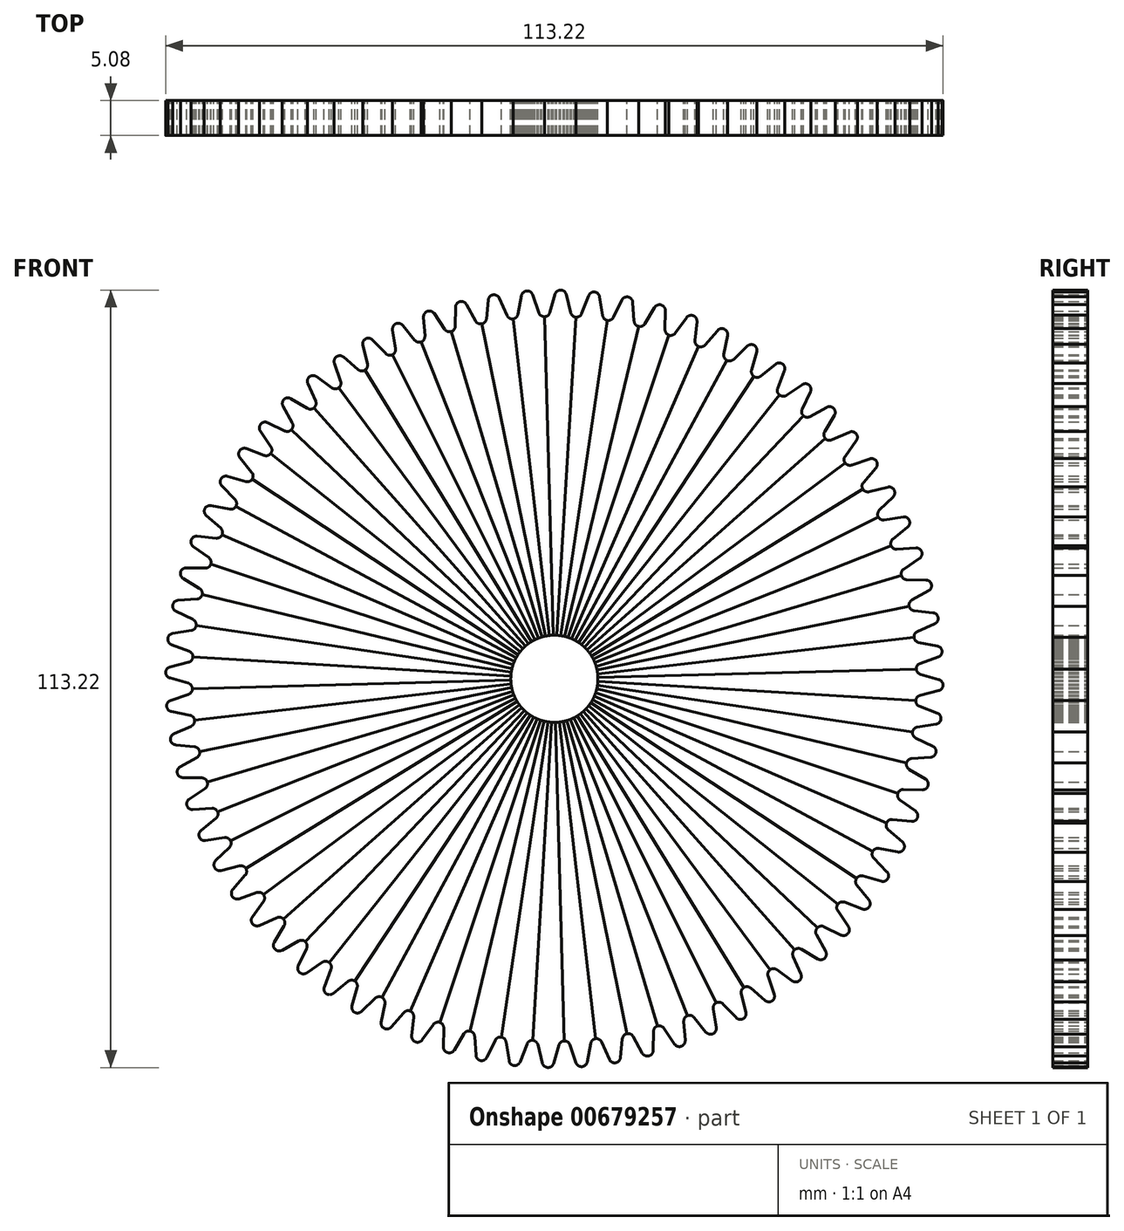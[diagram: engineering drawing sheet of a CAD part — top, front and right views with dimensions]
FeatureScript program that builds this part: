
annotation { "Feature Type Name" : "Feature", "Feature Type Description" : "" }
export const myFeature = defineFeature(function(context is Context, id is Id, definition is map)
    precondition{}
    {
        {
            var Q0;
            Q0=qCreatedBy(makeId("Front.planeOp"),FACE);
            var sketch = newSketch(context, id + "F0", { "sketchPlane" : qUnion([Q0])});
            skLineSegment(sketch, "E0", {"start": v(0, 0) * mm, "end": v(-33.7, 38.01) * mm});
            skLineSegment(sketch, "E1", {"start": v(-34.78, 40.44) * mm, "end": v(-35.92, 42.97) * mm});
            skLineSegment(sketch, "E2", {"start": v(-34.66, 44) * mm, "end": v(-32.41, 42.36) * mm});
            skLineSegment(sketch, "E3", {"start": v(-30.26, 40.8) * mm, "end": v(0, 0) * mm});
            skPoint(sketch, "E4.visualSharp", {"position": v(-37.2, 45.83) * mm});
            skArc(sketch, "E4.filletArc", {"start": v(-34.66, 44) * mm, "mid": v(-35.68, 43.96) * mm, "end": v(-35.92, 42.97) * mm});
            skLineSegment(sketch, "E5", {"start": v(-30.12, 40.61) * mm, "end": v(-31.42, 42.37) * mm});
            skLineSegment(sketch, "E6", {"start": v(-33.7, 38.01) * mm, "end": v(-35.55, 40.1) * mm});
            skPoint(sketch, "E7.visualSharp", {"position": v(-33.7, 38.01) * mm});
            skArc(sketch, "E7.filletArc", {"start": v(-35, 39.47) * mm, "mid": v(-34.73, 39.92) * mm, "end": v(-34.78, 40.44) * mm});
            skPoint(sketch, "E8.visualSharp", {"position": v(-30.26, 40.8) * mm});
            skArc(sketch, "E8.filletArc", {"start": v(-32.41, 42.36) * mm, "mid": v(-31.92, 42.2) * mm, "end": v(-31.42, 42.37) * mm});
            skPoint(sketch, "E9", {"position": v(-35, 39.47) * mm});
            skPoint(sketch, "E10", {"position": v(-31.42, 42.37) * mm});
            skSolve(sketch);
        }
        {
            var Q0;
            Q0=makeQuery(id+"F0.imprint","IMPRINT",FACE,{"disambiguationData":[TD([[makeQuery(id+"F0.imprint","IMPRINT",EDGE,{"derivedFrom":sQuery(id+"F0.wireOp",EDGE,"E0")}),-1.0]])]});
            extrude(context, id + "F1", {"entities" : qUnion([Q0]), "depth" : 5.08 * mm, "offsetDistance" : 25.4 * mm});
        }
        {
            var Q0;
            Q0=makeQuery(id+"F1.opExtrude","SWEPT_BODY",BODY,{"disambiguationData":[OSD([sQuery(id+"F0.wireOp",EDGE,"E0"),sQuery(id+"F0.wireOp",EDGE,"E1"),sQuery(id+"F0.wireOp",EDGE,"E2"),sQuery(id+"F0.wireOp",EDGE,"E3"),sQuery(id+"F0.wireOp",EDGE,"E4.filletArc"),sQuery(id+"F0.wireOp",EDGE,"E5"),sQuery(id+"F0.wireOp",EDGE,"E6"),sQuery(id+"F0.wireOp",EDGE,"E7.filletArc"),sQuery(id+"F0.wireOp",EDGE,"E8.filletArc")])]});
            var Q1;
            Q1=makeQuery(id+"F1.opExtrude","SWEPT_EDGE",EDGE,{"disambiguationData":[OSD([sQuery(id+"F0.wireOp",EDGE,"E0"),sQuery(id+"F0.wireOp",EDGE,"E3")])]});
            circularPattern(context, id + "F2", {"entities" : qUnion([Q0]), "axis" : qUnion([Q1]), "angle" : 360 * degree, "instanceCount" : 72, "equalSpace" : true});
        }
        {
            var Q0;
            Q0=sQuery(id+"F0.wireOp",VERTEX,"E3.end");
            var Q1;
            Q1=makeQuery(id+"F1.opExtrude","SWEPT_BODY",BODY,{"disambiguationData":[OSD([sQuery(id+"F0.wireOp",EDGE,"E0"),sQuery(id+"F0.wireOp",EDGE,"E1"),sQuery(id+"F0.wireOp",EDGE,"E2"),sQuery(id+"F0.wireOp",EDGE,"E3"),sQuery(id+"F0.wireOp",EDGE,"E4.filletArc"),sQuery(id+"F0.wireOp",EDGE,"E5"),sQuery(id+"F0.wireOp",EDGE,"E6"),sQuery(id+"F0.wireOp",EDGE,"E7.filletArc"),sQuery(id+"F0.wireOp",EDGE,"E8.filletArc")])]});
            var Q2;
            Q2=makeQuery(id+"F2.opPattern","COPY",BODY,{"derivedFrom":makeQuery(id+"F1.opExtrude","SWEPT_BODY",BODY,{"disambiguationData":[OSD([sQuery(id+"F0.wireOp",EDGE,"E0"),sQuery(id+"F0.wireOp",EDGE,"E1"),sQuery(id+"F0.wireOp",EDGE,"E2"),sQuery(id+"F0.wireOp",EDGE,"E3"),sQuery(id+"F0.wireOp",EDGE,"E4.filletArc"),sQuery(id+"F0.wireOp",EDGE,"E5"),sQuery(id+"F0.wireOp",EDGE,"E6"),sQuery(id+"F0.wireOp",EDGE,"E7.filletArc"),sQuery(id+"F0.wireOp",EDGE,"E8.filletArc")])]}),"instanceName":"1"});
            var Q3;
            Q3=makeQuery(id+"F2.opPattern","COPY",BODY,{"derivedFrom":makeQuery(id+"F1.opExtrude","SWEPT_BODY",BODY,{"disambiguationData":[OSD([sQuery(id+"F0.wireOp",EDGE,"E0"),sQuery(id+"F0.wireOp",EDGE,"E1"),sQuery(id+"F0.wireOp",EDGE,"E2"),sQuery(id+"F0.wireOp",EDGE,"E3"),sQuery(id+"F0.wireOp",EDGE,"E4.filletArc"),sQuery(id+"F0.wireOp",EDGE,"E5"),sQuery(id+"F0.wireOp",EDGE,"E6"),sQuery(id+"F0.wireOp",EDGE,"E7.filletArc"),sQuery(id+"F0.wireOp",EDGE,"E8.filletArc")])]}),"instanceName":"2"});
            var Q4;
            Q4=makeQuery(id+"F2.opPattern","COPY",BODY,{"derivedFrom":makeQuery(id+"F1.opExtrude","SWEPT_BODY",BODY,{"disambiguationData":[OSD([sQuery(id+"F0.wireOp",EDGE,"E0"),sQuery(id+"F0.wireOp",EDGE,"E1"),sQuery(id+"F0.wireOp",EDGE,"E2"),sQuery(id+"F0.wireOp",EDGE,"E3"),sQuery(id+"F0.wireOp",EDGE,"E4.filletArc"),sQuery(id+"F0.wireOp",EDGE,"E5"),sQuery(id+"F0.wireOp",EDGE,"E6"),sQuery(id+"F0.wireOp",EDGE,"E7.filletArc"),sQuery(id+"F0.wireOp",EDGE,"E8.filletArc")])]}),"instanceName":"3"});
            var Q5;
            Q5=makeQuery(id+"F2.opPattern","COPY",BODY,{"derivedFrom":makeQuery(id+"F1.opExtrude","SWEPT_BODY",BODY,{"disambiguationData":[OSD([sQuery(id+"F0.wireOp",EDGE,"E0"),sQuery(id+"F0.wireOp",EDGE,"E1"),sQuery(id+"F0.wireOp",EDGE,"E2"),sQuery(id+"F0.wireOp",EDGE,"E3"),sQuery(id+"F0.wireOp",EDGE,"E4.filletArc"),sQuery(id+"F0.wireOp",EDGE,"E5"),sQuery(id+"F0.wireOp",EDGE,"E6"),sQuery(id+"F0.wireOp",EDGE,"E7.filletArc"),sQuery(id+"F0.wireOp",EDGE,"E8.filletArc")])]}),"instanceName":"4"});
            var Q6;
            Q6=makeQuery(id+"F2.opPattern","COPY",BODY,{"derivedFrom":makeQuery(id+"F1.opExtrude","SWEPT_BODY",BODY,{"disambiguationData":[OSD([sQuery(id+"F0.wireOp",EDGE,"E0"),sQuery(id+"F0.wireOp",EDGE,"E1"),sQuery(id+"F0.wireOp",EDGE,"E2"),sQuery(id+"F0.wireOp",EDGE,"E3"),sQuery(id+"F0.wireOp",EDGE,"E4.filletArc"),sQuery(id+"F0.wireOp",EDGE,"E5"),sQuery(id+"F0.wireOp",EDGE,"E6"),sQuery(id+"F0.wireOp",EDGE,"E7.filletArc"),sQuery(id+"F0.wireOp",EDGE,"E8.filletArc")])]}),"instanceName":"5"});
            var Q7;
            Q7=makeQuery(id+"F2.opPattern","COPY",BODY,{"derivedFrom":makeQuery(id+"F1.opExtrude","SWEPT_BODY",BODY,{"disambiguationData":[OSD([sQuery(id+"F0.wireOp",EDGE,"E0"),sQuery(id+"F0.wireOp",EDGE,"E1"),sQuery(id+"F0.wireOp",EDGE,"E2"),sQuery(id+"F0.wireOp",EDGE,"E3"),sQuery(id+"F0.wireOp",EDGE,"E4.filletArc"),sQuery(id+"F0.wireOp",EDGE,"E5"),sQuery(id+"F0.wireOp",EDGE,"E6"),sQuery(id+"F0.wireOp",EDGE,"E7.filletArc"),sQuery(id+"F0.wireOp",EDGE,"E8.filletArc")])]}),"instanceName":"6"});
            var Q8;
            Q8=makeQuery(id+"F2.opPattern","COPY",BODY,{"derivedFrom":makeQuery(id+"F1.opExtrude","SWEPT_BODY",BODY,{"disambiguationData":[OSD([sQuery(id+"F0.wireOp",EDGE,"E0"),sQuery(id+"F0.wireOp",EDGE,"E1"),sQuery(id+"F0.wireOp",EDGE,"E2"),sQuery(id+"F0.wireOp",EDGE,"E3"),sQuery(id+"F0.wireOp",EDGE,"E4.filletArc"),sQuery(id+"F0.wireOp",EDGE,"E5"),sQuery(id+"F0.wireOp",EDGE,"E6"),sQuery(id+"F0.wireOp",EDGE,"E7.filletArc"),sQuery(id+"F0.wireOp",EDGE,"E8.filletArc")])]}),"instanceName":"7"});
            var Q9;
            Q9=makeQuery(id+"F2.opPattern","COPY",BODY,{"derivedFrom":makeQuery(id+"F1.opExtrude","SWEPT_BODY",BODY,{"disambiguationData":[OSD([sQuery(id+"F0.wireOp",EDGE,"E0"),sQuery(id+"F0.wireOp",EDGE,"E1"),sQuery(id+"F0.wireOp",EDGE,"E2"),sQuery(id+"F0.wireOp",EDGE,"E3"),sQuery(id+"F0.wireOp",EDGE,"E4.filletArc"),sQuery(id+"F0.wireOp",EDGE,"E5"),sQuery(id+"F0.wireOp",EDGE,"E6"),sQuery(id+"F0.wireOp",EDGE,"E7.filletArc"),sQuery(id+"F0.wireOp",EDGE,"E8.filletArc")])]}),"instanceName":"8"});
            var Q10;
            Q10=makeQuery(id+"F2.opPattern","COPY",BODY,{"derivedFrom":makeQuery(id+"F1.opExtrude","SWEPT_BODY",BODY,{"disambiguationData":[OSD([sQuery(id+"F0.wireOp",EDGE,"E0"),sQuery(id+"F0.wireOp",EDGE,"E1"),sQuery(id+"F0.wireOp",EDGE,"E2"),sQuery(id+"F0.wireOp",EDGE,"E3"),sQuery(id+"F0.wireOp",EDGE,"E4.filletArc"),sQuery(id+"F0.wireOp",EDGE,"E5"),sQuery(id+"F0.wireOp",EDGE,"E6"),sQuery(id+"F0.wireOp",EDGE,"E7.filletArc"),sQuery(id+"F0.wireOp",EDGE,"E8.filletArc")])]}),"instanceName":"9"});
            var Q11;
            Q11=makeQuery(id+"F2.opPattern","COPY",BODY,{"derivedFrom":makeQuery(id+"F1.opExtrude","SWEPT_BODY",BODY,{"disambiguationData":[OSD([sQuery(id+"F0.wireOp",EDGE,"E0"),sQuery(id+"F0.wireOp",EDGE,"E1"),sQuery(id+"F0.wireOp",EDGE,"E2"),sQuery(id+"F0.wireOp",EDGE,"E3"),sQuery(id+"F0.wireOp",EDGE,"E4.filletArc"),sQuery(id+"F0.wireOp",EDGE,"E5"),sQuery(id+"F0.wireOp",EDGE,"E6"),sQuery(id+"F0.wireOp",EDGE,"E7.filletArc"),sQuery(id+"F0.wireOp",EDGE,"E8.filletArc")])]}),"instanceName":"10"});
            var Q12;
            Q12=makeQuery(id+"F2.opPattern","COPY",BODY,{"derivedFrom":makeQuery(id+"F1.opExtrude","SWEPT_BODY",BODY,{"disambiguationData":[OSD([sQuery(id+"F0.wireOp",EDGE,"E0"),sQuery(id+"F0.wireOp",EDGE,"E1"),sQuery(id+"F0.wireOp",EDGE,"E2"),sQuery(id+"F0.wireOp",EDGE,"E3"),sQuery(id+"F0.wireOp",EDGE,"E4.filletArc"),sQuery(id+"F0.wireOp",EDGE,"E5"),sQuery(id+"F0.wireOp",EDGE,"E6"),sQuery(id+"F0.wireOp",EDGE,"E7.filletArc"),sQuery(id+"F0.wireOp",EDGE,"E8.filletArc")])]}),"instanceName":"11"});
            var Q13;
            Q13=makeQuery(id+"F2.opPattern","COPY",BODY,{"derivedFrom":makeQuery(id+"F1.opExtrude","SWEPT_BODY",BODY,{"disambiguationData":[OSD([sQuery(id+"F0.wireOp",EDGE,"E0"),sQuery(id+"F0.wireOp",EDGE,"E1"),sQuery(id+"F0.wireOp",EDGE,"E2"),sQuery(id+"F0.wireOp",EDGE,"E3"),sQuery(id+"F0.wireOp",EDGE,"E4.filletArc"),sQuery(id+"F0.wireOp",EDGE,"E5"),sQuery(id+"F0.wireOp",EDGE,"E6"),sQuery(id+"F0.wireOp",EDGE,"E7.filletArc"),sQuery(id+"F0.wireOp",EDGE,"E8.filletArc")])]}),"instanceName":"12"});
            var Q14;
            Q14=makeQuery(id+"F2.opPattern","COPY",BODY,{"derivedFrom":makeQuery(id+"F1.opExtrude","SWEPT_BODY",BODY,{"disambiguationData":[OSD([sQuery(id+"F0.wireOp",EDGE,"E0"),sQuery(id+"F0.wireOp",EDGE,"E1"),sQuery(id+"F0.wireOp",EDGE,"E2"),sQuery(id+"F0.wireOp",EDGE,"E3"),sQuery(id+"F0.wireOp",EDGE,"E4.filletArc"),sQuery(id+"F0.wireOp",EDGE,"E5"),sQuery(id+"F0.wireOp",EDGE,"E6"),sQuery(id+"F0.wireOp",EDGE,"E7.filletArc"),sQuery(id+"F0.wireOp",EDGE,"E8.filletArc")])]}),"instanceName":"13"});
            var Q15;
            Q15=makeQuery(id+"F2.opPattern","COPY",BODY,{"derivedFrom":makeQuery(id+"F1.opExtrude","SWEPT_BODY",BODY,{"disambiguationData":[OSD([sQuery(id+"F0.wireOp",EDGE,"E0"),sQuery(id+"F0.wireOp",EDGE,"E1"),sQuery(id+"F0.wireOp",EDGE,"E2"),sQuery(id+"F0.wireOp",EDGE,"E3"),sQuery(id+"F0.wireOp",EDGE,"E4.filletArc"),sQuery(id+"F0.wireOp",EDGE,"E5"),sQuery(id+"F0.wireOp",EDGE,"E6"),sQuery(id+"F0.wireOp",EDGE,"E7.filletArc"),sQuery(id+"F0.wireOp",EDGE,"E8.filletArc")])]}),"instanceName":"14"});
            var Q16;
            Q16=makeQuery(id+"F2.opPattern","COPY",BODY,{"derivedFrom":makeQuery(id+"F1.opExtrude","SWEPT_BODY",BODY,{"disambiguationData":[OSD([sQuery(id+"F0.wireOp",EDGE,"E0"),sQuery(id+"F0.wireOp",EDGE,"E1"),sQuery(id+"F0.wireOp",EDGE,"E2"),sQuery(id+"F0.wireOp",EDGE,"E3"),sQuery(id+"F0.wireOp",EDGE,"E4.filletArc"),sQuery(id+"F0.wireOp",EDGE,"E5"),sQuery(id+"F0.wireOp",EDGE,"E6"),sQuery(id+"F0.wireOp",EDGE,"E7.filletArc"),sQuery(id+"F0.wireOp",EDGE,"E8.filletArc")])]}),"instanceName":"15"});
            var Q17;
            Q17=makeQuery(id+"F2.opPattern","COPY",BODY,{"derivedFrom":makeQuery(id+"F1.opExtrude","SWEPT_BODY",BODY,{"disambiguationData":[OSD([sQuery(id+"F0.wireOp",EDGE,"E0"),sQuery(id+"F0.wireOp",EDGE,"E1"),sQuery(id+"F0.wireOp",EDGE,"E2"),sQuery(id+"F0.wireOp",EDGE,"E3"),sQuery(id+"F0.wireOp",EDGE,"E4.filletArc"),sQuery(id+"F0.wireOp",EDGE,"E5"),sQuery(id+"F0.wireOp",EDGE,"E6"),sQuery(id+"F0.wireOp",EDGE,"E7.filletArc"),sQuery(id+"F0.wireOp",EDGE,"E8.filletArc")])]}),"instanceName":"16"});
            var Q18;
            Q18=makeQuery(id+"F2.opPattern","COPY",BODY,{"derivedFrom":makeQuery(id+"F1.opExtrude","SWEPT_BODY",BODY,{"disambiguationData":[OSD([sQuery(id+"F0.wireOp",EDGE,"E0"),sQuery(id+"F0.wireOp",EDGE,"E1"),sQuery(id+"F0.wireOp",EDGE,"E2"),sQuery(id+"F0.wireOp",EDGE,"E3"),sQuery(id+"F0.wireOp",EDGE,"E4.filletArc"),sQuery(id+"F0.wireOp",EDGE,"E5"),sQuery(id+"F0.wireOp",EDGE,"E6"),sQuery(id+"F0.wireOp",EDGE,"E7.filletArc"),sQuery(id+"F0.wireOp",EDGE,"E8.filletArc")])]}),"instanceName":"17"});
            var Q19;
            Q19=makeQuery(id+"F2.opPattern","COPY",BODY,{"derivedFrom":makeQuery(id+"F1.opExtrude","SWEPT_BODY",BODY,{"disambiguationData":[OSD([sQuery(id+"F0.wireOp",EDGE,"E0"),sQuery(id+"F0.wireOp",EDGE,"E1"),sQuery(id+"F0.wireOp",EDGE,"E2"),sQuery(id+"F0.wireOp",EDGE,"E3"),sQuery(id+"F0.wireOp",EDGE,"E4.filletArc"),sQuery(id+"F0.wireOp",EDGE,"E5"),sQuery(id+"F0.wireOp",EDGE,"E6"),sQuery(id+"F0.wireOp",EDGE,"E7.filletArc"),sQuery(id+"F0.wireOp",EDGE,"E8.filletArc")])]}),"instanceName":"18"});
            var Q20;
            Q20=makeQuery(id+"F2.opPattern","COPY",BODY,{"derivedFrom":makeQuery(id+"F1.opExtrude","SWEPT_BODY",BODY,{"disambiguationData":[OSD([sQuery(id+"F0.wireOp",EDGE,"E0"),sQuery(id+"F0.wireOp",EDGE,"E1"),sQuery(id+"F0.wireOp",EDGE,"E2"),sQuery(id+"F0.wireOp",EDGE,"E3"),sQuery(id+"F0.wireOp",EDGE,"E4.filletArc"),sQuery(id+"F0.wireOp",EDGE,"E5"),sQuery(id+"F0.wireOp",EDGE,"E6"),sQuery(id+"F0.wireOp",EDGE,"E7.filletArc"),sQuery(id+"F0.wireOp",EDGE,"E8.filletArc")])]}),"instanceName":"19"});
            var Q21;
            Q21=makeQuery(id+"F2.opPattern","COPY",BODY,{"derivedFrom":makeQuery(id+"F1.opExtrude","SWEPT_BODY",BODY,{"disambiguationData":[OSD([sQuery(id+"F0.wireOp",EDGE,"E0"),sQuery(id+"F0.wireOp",EDGE,"E1"),sQuery(id+"F0.wireOp",EDGE,"E2"),sQuery(id+"F0.wireOp",EDGE,"E3"),sQuery(id+"F0.wireOp",EDGE,"E4.filletArc"),sQuery(id+"F0.wireOp",EDGE,"E5"),sQuery(id+"F0.wireOp",EDGE,"E6"),sQuery(id+"F0.wireOp",EDGE,"E7.filletArc"),sQuery(id+"F0.wireOp",EDGE,"E8.filletArc")])]}),"instanceName":"20"});
            var Q22;
            Q22=makeQuery(id+"F2.opPattern","COPY",BODY,{"derivedFrom":makeQuery(id+"F1.opExtrude","SWEPT_BODY",BODY,{"disambiguationData":[OSD([sQuery(id+"F0.wireOp",EDGE,"E0"),sQuery(id+"F0.wireOp",EDGE,"E1"),sQuery(id+"F0.wireOp",EDGE,"E2"),sQuery(id+"F0.wireOp",EDGE,"E3"),sQuery(id+"F0.wireOp",EDGE,"E4.filletArc"),sQuery(id+"F0.wireOp",EDGE,"E5"),sQuery(id+"F0.wireOp",EDGE,"E6"),sQuery(id+"F0.wireOp",EDGE,"E7.filletArc"),sQuery(id+"F0.wireOp",EDGE,"E8.filletArc")])]}),"instanceName":"21"});
            var Q23;
            Q23=makeQuery(id+"F2.opPattern","COPY",BODY,{"derivedFrom":makeQuery(id+"F1.opExtrude","SWEPT_BODY",BODY,{"disambiguationData":[OSD([sQuery(id+"F0.wireOp",EDGE,"E0"),sQuery(id+"F0.wireOp",EDGE,"E1"),sQuery(id+"F0.wireOp",EDGE,"E2"),sQuery(id+"F0.wireOp",EDGE,"E3"),sQuery(id+"F0.wireOp",EDGE,"E4.filletArc"),sQuery(id+"F0.wireOp",EDGE,"E5"),sQuery(id+"F0.wireOp",EDGE,"E6"),sQuery(id+"F0.wireOp",EDGE,"E7.filletArc"),sQuery(id+"F0.wireOp",EDGE,"E8.filletArc")])]}),"instanceName":"22"});
            var Q24;
            Q24=makeQuery(id+"F2.opPattern","COPY",BODY,{"derivedFrom":makeQuery(id+"F1.opExtrude","SWEPT_BODY",BODY,{"disambiguationData":[OSD([sQuery(id+"F0.wireOp",EDGE,"E0"),sQuery(id+"F0.wireOp",EDGE,"E1"),sQuery(id+"F0.wireOp",EDGE,"E2"),sQuery(id+"F0.wireOp",EDGE,"E3"),sQuery(id+"F0.wireOp",EDGE,"E4.filletArc"),sQuery(id+"F0.wireOp",EDGE,"E5"),sQuery(id+"F0.wireOp",EDGE,"E6"),sQuery(id+"F0.wireOp",EDGE,"E7.filletArc"),sQuery(id+"F0.wireOp",EDGE,"E8.filletArc")])]}),"instanceName":"23"});
            var Q25;
            Q25=makeQuery(id+"F2.opPattern","COPY",BODY,{"derivedFrom":makeQuery(id+"F1.opExtrude","SWEPT_BODY",BODY,{"disambiguationData":[OSD([sQuery(id+"F0.wireOp",EDGE,"E0"),sQuery(id+"F0.wireOp",EDGE,"E1"),sQuery(id+"F0.wireOp",EDGE,"E2"),sQuery(id+"F0.wireOp",EDGE,"E3"),sQuery(id+"F0.wireOp",EDGE,"E4.filletArc"),sQuery(id+"F0.wireOp",EDGE,"E5"),sQuery(id+"F0.wireOp",EDGE,"E6"),sQuery(id+"F0.wireOp",EDGE,"E7.filletArc"),sQuery(id+"F0.wireOp",EDGE,"E8.filletArc")])]}),"instanceName":"24"});
            var Q26;
            Q26=makeQuery(id+"F2.opPattern","COPY",BODY,{"derivedFrom":makeQuery(id+"F1.opExtrude","SWEPT_BODY",BODY,{"disambiguationData":[OSD([sQuery(id+"F0.wireOp",EDGE,"E0"),sQuery(id+"F0.wireOp",EDGE,"E1"),sQuery(id+"F0.wireOp",EDGE,"E2"),sQuery(id+"F0.wireOp",EDGE,"E3"),sQuery(id+"F0.wireOp",EDGE,"E4.filletArc"),sQuery(id+"F0.wireOp",EDGE,"E5"),sQuery(id+"F0.wireOp",EDGE,"E6"),sQuery(id+"F0.wireOp",EDGE,"E7.filletArc"),sQuery(id+"F0.wireOp",EDGE,"E8.filletArc")])]}),"instanceName":"25"});
            var Q27;
            Q27=makeQuery(id+"F2.opPattern","COPY",BODY,{"derivedFrom":makeQuery(id+"F1.opExtrude","SWEPT_BODY",BODY,{"disambiguationData":[OSD([sQuery(id+"F0.wireOp",EDGE,"E0"),sQuery(id+"F0.wireOp",EDGE,"E1"),sQuery(id+"F0.wireOp",EDGE,"E2"),sQuery(id+"F0.wireOp",EDGE,"E3"),sQuery(id+"F0.wireOp",EDGE,"E4.filletArc"),sQuery(id+"F0.wireOp",EDGE,"E5"),sQuery(id+"F0.wireOp",EDGE,"E6"),sQuery(id+"F0.wireOp",EDGE,"E7.filletArc"),sQuery(id+"F0.wireOp",EDGE,"E8.filletArc")])]}),"instanceName":"26"});
            var Q28;
            Q28=makeQuery(id+"F2.opPattern","COPY",BODY,{"derivedFrom":makeQuery(id+"F1.opExtrude","SWEPT_BODY",BODY,{"disambiguationData":[OSD([sQuery(id+"F0.wireOp",EDGE,"E0"),sQuery(id+"F0.wireOp",EDGE,"E1"),sQuery(id+"F0.wireOp",EDGE,"E2"),sQuery(id+"F0.wireOp",EDGE,"E3"),sQuery(id+"F0.wireOp",EDGE,"E4.filletArc"),sQuery(id+"F0.wireOp",EDGE,"E5"),sQuery(id+"F0.wireOp",EDGE,"E6"),sQuery(id+"F0.wireOp",EDGE,"E7.filletArc"),sQuery(id+"F0.wireOp",EDGE,"E8.filletArc")])]}),"instanceName":"27"});
            var Q29;
            Q29=makeQuery(id+"F2.opPattern","COPY",BODY,{"derivedFrom":makeQuery(id+"F1.opExtrude","SWEPT_BODY",BODY,{"disambiguationData":[OSD([sQuery(id+"F0.wireOp",EDGE,"E0"),sQuery(id+"F0.wireOp",EDGE,"E1"),sQuery(id+"F0.wireOp",EDGE,"E2"),sQuery(id+"F0.wireOp",EDGE,"E3"),sQuery(id+"F0.wireOp",EDGE,"E4.filletArc"),sQuery(id+"F0.wireOp",EDGE,"E5"),sQuery(id+"F0.wireOp",EDGE,"E6"),sQuery(id+"F0.wireOp",EDGE,"E7.filletArc"),sQuery(id+"F0.wireOp",EDGE,"E8.filletArc")])]}),"instanceName":"28"});
            var Q30;
            Q30=makeQuery(id+"F2.opPattern","COPY",BODY,{"derivedFrom":makeQuery(id+"F1.opExtrude","SWEPT_BODY",BODY,{"disambiguationData":[OSD([sQuery(id+"F0.wireOp",EDGE,"E0"),sQuery(id+"F0.wireOp",EDGE,"E1"),sQuery(id+"F0.wireOp",EDGE,"E2"),sQuery(id+"F0.wireOp",EDGE,"E3"),sQuery(id+"F0.wireOp",EDGE,"E4.filletArc"),sQuery(id+"F0.wireOp",EDGE,"E5"),sQuery(id+"F0.wireOp",EDGE,"E6"),sQuery(id+"F0.wireOp",EDGE,"E7.filletArc"),sQuery(id+"F0.wireOp",EDGE,"E8.filletArc")])]}),"instanceName":"29"});
            var Q31;
            Q31=makeQuery(id+"F2.opPattern","COPY",BODY,{"derivedFrom":makeQuery(id+"F1.opExtrude","SWEPT_BODY",BODY,{"disambiguationData":[OSD([sQuery(id+"F0.wireOp",EDGE,"E0"),sQuery(id+"F0.wireOp",EDGE,"E1"),sQuery(id+"F0.wireOp",EDGE,"E2"),sQuery(id+"F0.wireOp",EDGE,"E3"),sQuery(id+"F0.wireOp",EDGE,"E4.filletArc"),sQuery(id+"F0.wireOp",EDGE,"E5"),sQuery(id+"F0.wireOp",EDGE,"E6"),sQuery(id+"F0.wireOp",EDGE,"E7.filletArc"),sQuery(id+"F0.wireOp",EDGE,"E8.filletArc")])]}),"instanceName":"30"});
            var Q32;
            Q32=makeQuery(id+"F2.opPattern","COPY",BODY,{"derivedFrom":makeQuery(id+"F1.opExtrude","SWEPT_BODY",BODY,{"disambiguationData":[OSD([sQuery(id+"F0.wireOp",EDGE,"E0"),sQuery(id+"F0.wireOp",EDGE,"E1"),sQuery(id+"F0.wireOp",EDGE,"E2"),sQuery(id+"F0.wireOp",EDGE,"E3"),sQuery(id+"F0.wireOp",EDGE,"E4.filletArc"),sQuery(id+"F0.wireOp",EDGE,"E5"),sQuery(id+"F0.wireOp",EDGE,"E6"),sQuery(id+"F0.wireOp",EDGE,"E7.filletArc"),sQuery(id+"F0.wireOp",EDGE,"E8.filletArc")])]}),"instanceName":"31"});
            var Q33;
            Q33=makeQuery(id+"F2.opPattern","COPY",BODY,{"derivedFrom":makeQuery(id+"F1.opExtrude","SWEPT_BODY",BODY,{"disambiguationData":[OSD([sQuery(id+"F0.wireOp",EDGE,"E0"),sQuery(id+"F0.wireOp",EDGE,"E1"),sQuery(id+"F0.wireOp",EDGE,"E2"),sQuery(id+"F0.wireOp",EDGE,"E3"),sQuery(id+"F0.wireOp",EDGE,"E4.filletArc"),sQuery(id+"F0.wireOp",EDGE,"E5"),sQuery(id+"F0.wireOp",EDGE,"E6"),sQuery(id+"F0.wireOp",EDGE,"E7.filletArc"),sQuery(id+"F0.wireOp",EDGE,"E8.filletArc")])]}),"instanceName":"32"});
            var Q34;
            Q34=makeQuery(id+"F2.opPattern","COPY",BODY,{"derivedFrom":makeQuery(id+"F1.opExtrude","SWEPT_BODY",BODY,{"disambiguationData":[OSD([sQuery(id+"F0.wireOp",EDGE,"E0"),sQuery(id+"F0.wireOp",EDGE,"E1"),sQuery(id+"F0.wireOp",EDGE,"E2"),sQuery(id+"F0.wireOp",EDGE,"E3"),sQuery(id+"F0.wireOp",EDGE,"E4.filletArc"),sQuery(id+"F0.wireOp",EDGE,"E5"),sQuery(id+"F0.wireOp",EDGE,"E6"),sQuery(id+"F0.wireOp",EDGE,"E7.filletArc"),sQuery(id+"F0.wireOp",EDGE,"E8.filletArc")])]}),"instanceName":"33"});
            var Q35;
            Q35=makeQuery(id+"F2.opPattern","COPY",BODY,{"derivedFrom":makeQuery(id+"F1.opExtrude","SWEPT_BODY",BODY,{"disambiguationData":[OSD([sQuery(id+"F0.wireOp",EDGE,"E0"),sQuery(id+"F0.wireOp",EDGE,"E1"),sQuery(id+"F0.wireOp",EDGE,"E2"),sQuery(id+"F0.wireOp",EDGE,"E3"),sQuery(id+"F0.wireOp",EDGE,"E4.filletArc"),sQuery(id+"F0.wireOp",EDGE,"E5"),sQuery(id+"F0.wireOp",EDGE,"E6"),sQuery(id+"F0.wireOp",EDGE,"E7.filletArc"),sQuery(id+"F0.wireOp",EDGE,"E8.filletArc")])]}),"instanceName":"34"});
            var Q36;
            Q36=makeQuery(id+"F2.opPattern","COPY",BODY,{"derivedFrom":makeQuery(id+"F1.opExtrude","SWEPT_BODY",BODY,{"disambiguationData":[OSD([sQuery(id+"F0.wireOp",EDGE,"E0"),sQuery(id+"F0.wireOp",EDGE,"E1"),sQuery(id+"F0.wireOp",EDGE,"E2"),sQuery(id+"F0.wireOp",EDGE,"E3"),sQuery(id+"F0.wireOp",EDGE,"E4.filletArc"),sQuery(id+"F0.wireOp",EDGE,"E5"),sQuery(id+"F0.wireOp",EDGE,"E6"),sQuery(id+"F0.wireOp",EDGE,"E7.filletArc"),sQuery(id+"F0.wireOp",EDGE,"E8.filletArc")])]}),"instanceName":"35"});
            var Q37;
            Q37=makeQuery(id+"F2.opPattern","COPY",BODY,{"derivedFrom":makeQuery(id+"F1.opExtrude","SWEPT_BODY",BODY,{"disambiguationData":[OSD([sQuery(id+"F0.wireOp",EDGE,"E0"),sQuery(id+"F0.wireOp",EDGE,"E1"),sQuery(id+"F0.wireOp",EDGE,"E2"),sQuery(id+"F0.wireOp",EDGE,"E3"),sQuery(id+"F0.wireOp",EDGE,"E4.filletArc"),sQuery(id+"F0.wireOp",EDGE,"E5"),sQuery(id+"F0.wireOp",EDGE,"E6"),sQuery(id+"F0.wireOp",EDGE,"E7.filletArc"),sQuery(id+"F0.wireOp",EDGE,"E8.filletArc")])]}),"instanceName":"36"});
            var Q38;
            Q38=makeQuery(id+"F2.opPattern","COPY",BODY,{"derivedFrom":makeQuery(id+"F1.opExtrude","SWEPT_BODY",BODY,{"disambiguationData":[OSD([sQuery(id+"F0.wireOp",EDGE,"E0"),sQuery(id+"F0.wireOp",EDGE,"E1"),sQuery(id+"F0.wireOp",EDGE,"E2"),sQuery(id+"F0.wireOp",EDGE,"E3"),sQuery(id+"F0.wireOp",EDGE,"E4.filletArc"),sQuery(id+"F0.wireOp",EDGE,"E5"),sQuery(id+"F0.wireOp",EDGE,"E6"),sQuery(id+"F0.wireOp",EDGE,"E7.filletArc"),sQuery(id+"F0.wireOp",EDGE,"E8.filletArc")])]}),"instanceName":"37"});
            var Q39;
            Q39=makeQuery(id+"F2.opPattern","COPY",BODY,{"derivedFrom":makeQuery(id+"F1.opExtrude","SWEPT_BODY",BODY,{"disambiguationData":[OSD([sQuery(id+"F0.wireOp",EDGE,"E0"),sQuery(id+"F0.wireOp",EDGE,"E1"),sQuery(id+"F0.wireOp",EDGE,"E2"),sQuery(id+"F0.wireOp",EDGE,"E3"),sQuery(id+"F0.wireOp",EDGE,"E4.filletArc"),sQuery(id+"F0.wireOp",EDGE,"E5"),sQuery(id+"F0.wireOp",EDGE,"E6"),sQuery(id+"F0.wireOp",EDGE,"E7.filletArc"),sQuery(id+"F0.wireOp",EDGE,"E8.filletArc")])]}),"instanceName":"38"});
            var Q40;
            Q40=makeQuery(id+"F2.opPattern","COPY",BODY,{"derivedFrom":makeQuery(id+"F1.opExtrude","SWEPT_BODY",BODY,{"disambiguationData":[OSD([sQuery(id+"F0.wireOp",EDGE,"E0"),sQuery(id+"F0.wireOp",EDGE,"E1"),sQuery(id+"F0.wireOp",EDGE,"E2"),sQuery(id+"F0.wireOp",EDGE,"E3"),sQuery(id+"F0.wireOp",EDGE,"E4.filletArc"),sQuery(id+"F0.wireOp",EDGE,"E5"),sQuery(id+"F0.wireOp",EDGE,"E6"),sQuery(id+"F0.wireOp",EDGE,"E7.filletArc"),sQuery(id+"F0.wireOp",EDGE,"E8.filletArc")])]}),"instanceName":"39"});
            var Q41;
            Q41=makeQuery(id+"F2.opPattern","COPY",BODY,{"derivedFrom":makeQuery(id+"F1.opExtrude","SWEPT_BODY",BODY,{"disambiguationData":[OSD([sQuery(id+"F0.wireOp",EDGE,"E0"),sQuery(id+"F0.wireOp",EDGE,"E1"),sQuery(id+"F0.wireOp",EDGE,"E2"),sQuery(id+"F0.wireOp",EDGE,"E3"),sQuery(id+"F0.wireOp",EDGE,"E4.filletArc"),sQuery(id+"F0.wireOp",EDGE,"E5"),sQuery(id+"F0.wireOp",EDGE,"E6"),sQuery(id+"F0.wireOp",EDGE,"E7.filletArc"),sQuery(id+"F0.wireOp",EDGE,"E8.filletArc")])]}),"instanceName":"40"});
            var Q42;
            Q42=makeQuery(id+"F2.opPattern","COPY",BODY,{"derivedFrom":makeQuery(id+"F1.opExtrude","SWEPT_BODY",BODY,{"disambiguationData":[OSD([sQuery(id+"F0.wireOp",EDGE,"E0"),sQuery(id+"F0.wireOp",EDGE,"E1"),sQuery(id+"F0.wireOp",EDGE,"E2"),sQuery(id+"F0.wireOp",EDGE,"E3"),sQuery(id+"F0.wireOp",EDGE,"E4.filletArc"),sQuery(id+"F0.wireOp",EDGE,"E5"),sQuery(id+"F0.wireOp",EDGE,"E6"),sQuery(id+"F0.wireOp",EDGE,"E7.filletArc"),sQuery(id+"F0.wireOp",EDGE,"E8.filletArc")])]}),"instanceName":"41"});
            var Q43;
            Q43=makeQuery(id+"F2.opPattern","COPY",BODY,{"derivedFrom":makeQuery(id+"F1.opExtrude","SWEPT_BODY",BODY,{"disambiguationData":[OSD([sQuery(id+"F0.wireOp",EDGE,"E0"),sQuery(id+"F0.wireOp",EDGE,"E1"),sQuery(id+"F0.wireOp",EDGE,"E2"),sQuery(id+"F0.wireOp",EDGE,"E3"),sQuery(id+"F0.wireOp",EDGE,"E4.filletArc"),sQuery(id+"F0.wireOp",EDGE,"E5"),sQuery(id+"F0.wireOp",EDGE,"E6"),sQuery(id+"F0.wireOp",EDGE,"E7.filletArc"),sQuery(id+"F0.wireOp",EDGE,"E8.filletArc")])]}),"instanceName":"42"});
            var Q44;
            Q44=makeQuery(id+"F2.opPattern","COPY",BODY,{"derivedFrom":makeQuery(id+"F1.opExtrude","SWEPT_BODY",BODY,{"disambiguationData":[OSD([sQuery(id+"F0.wireOp",EDGE,"E0"),sQuery(id+"F0.wireOp",EDGE,"E1"),sQuery(id+"F0.wireOp",EDGE,"E2"),sQuery(id+"F0.wireOp",EDGE,"E3"),sQuery(id+"F0.wireOp",EDGE,"E4.filletArc"),sQuery(id+"F0.wireOp",EDGE,"E5"),sQuery(id+"F0.wireOp",EDGE,"E6"),sQuery(id+"F0.wireOp",EDGE,"E7.filletArc"),sQuery(id+"F0.wireOp",EDGE,"E8.filletArc")])]}),"instanceName":"43"});
            var Q45;
            Q45=makeQuery(id+"F2.opPattern","COPY",BODY,{"derivedFrom":makeQuery(id+"F1.opExtrude","SWEPT_BODY",BODY,{"disambiguationData":[OSD([sQuery(id+"F0.wireOp",EDGE,"E0"),sQuery(id+"F0.wireOp",EDGE,"E1"),sQuery(id+"F0.wireOp",EDGE,"E2"),sQuery(id+"F0.wireOp",EDGE,"E3"),sQuery(id+"F0.wireOp",EDGE,"E4.filletArc"),sQuery(id+"F0.wireOp",EDGE,"E5"),sQuery(id+"F0.wireOp",EDGE,"E6"),sQuery(id+"F0.wireOp",EDGE,"E7.filletArc"),sQuery(id+"F0.wireOp",EDGE,"E8.filletArc")])]}),"instanceName":"44"});
            var Q46;
            Q46=makeQuery(id+"F2.opPattern","COPY",BODY,{"derivedFrom":makeQuery(id+"F1.opExtrude","SWEPT_BODY",BODY,{"disambiguationData":[OSD([sQuery(id+"F0.wireOp",EDGE,"E0"),sQuery(id+"F0.wireOp",EDGE,"E1"),sQuery(id+"F0.wireOp",EDGE,"E2"),sQuery(id+"F0.wireOp",EDGE,"E3"),sQuery(id+"F0.wireOp",EDGE,"E4.filletArc"),sQuery(id+"F0.wireOp",EDGE,"E5"),sQuery(id+"F0.wireOp",EDGE,"E6"),sQuery(id+"F0.wireOp",EDGE,"E7.filletArc"),sQuery(id+"F0.wireOp",EDGE,"E8.filletArc")])]}),"instanceName":"45"});
            var Q47;
            Q47=makeQuery(id+"F2.opPattern","COPY",BODY,{"derivedFrom":makeQuery(id+"F1.opExtrude","SWEPT_BODY",BODY,{"disambiguationData":[OSD([sQuery(id+"F0.wireOp",EDGE,"E0"),sQuery(id+"F0.wireOp",EDGE,"E1"),sQuery(id+"F0.wireOp",EDGE,"E2"),sQuery(id+"F0.wireOp",EDGE,"E3"),sQuery(id+"F0.wireOp",EDGE,"E4.filletArc"),sQuery(id+"F0.wireOp",EDGE,"E5"),sQuery(id+"F0.wireOp",EDGE,"E6"),sQuery(id+"F0.wireOp",EDGE,"E7.filletArc"),sQuery(id+"F0.wireOp",EDGE,"E8.filletArc")])]}),"instanceName":"46"});
            var Q48;
            Q48=makeQuery(id+"F2.opPattern","COPY",BODY,{"derivedFrom":makeQuery(id+"F1.opExtrude","SWEPT_BODY",BODY,{"disambiguationData":[OSD([sQuery(id+"F0.wireOp",EDGE,"E0"),sQuery(id+"F0.wireOp",EDGE,"E1"),sQuery(id+"F0.wireOp",EDGE,"E2"),sQuery(id+"F0.wireOp",EDGE,"E3"),sQuery(id+"F0.wireOp",EDGE,"E4.filletArc"),sQuery(id+"F0.wireOp",EDGE,"E5"),sQuery(id+"F0.wireOp",EDGE,"E6"),sQuery(id+"F0.wireOp",EDGE,"E7.filletArc"),sQuery(id+"F0.wireOp",EDGE,"E8.filletArc")])]}),"instanceName":"47"});
            var Q49;
            Q49=makeQuery(id+"F2.opPattern","COPY",BODY,{"derivedFrom":makeQuery(id+"F1.opExtrude","SWEPT_BODY",BODY,{"disambiguationData":[OSD([sQuery(id+"F0.wireOp",EDGE,"E0"),sQuery(id+"F0.wireOp",EDGE,"E1"),sQuery(id+"F0.wireOp",EDGE,"E2"),sQuery(id+"F0.wireOp",EDGE,"E3"),sQuery(id+"F0.wireOp",EDGE,"E4.filletArc"),sQuery(id+"F0.wireOp",EDGE,"E5"),sQuery(id+"F0.wireOp",EDGE,"E6"),sQuery(id+"F0.wireOp",EDGE,"E7.filletArc"),sQuery(id+"F0.wireOp",EDGE,"E8.filletArc")])]}),"instanceName":"48"});
            var Q50;
            Q50=makeQuery(id+"F2.opPattern","COPY",BODY,{"derivedFrom":makeQuery(id+"F1.opExtrude","SWEPT_BODY",BODY,{"disambiguationData":[OSD([sQuery(id+"F0.wireOp",EDGE,"E0"),sQuery(id+"F0.wireOp",EDGE,"E1"),sQuery(id+"F0.wireOp",EDGE,"E2"),sQuery(id+"F0.wireOp",EDGE,"E3"),sQuery(id+"F0.wireOp",EDGE,"E4.filletArc"),sQuery(id+"F0.wireOp",EDGE,"E5"),sQuery(id+"F0.wireOp",EDGE,"E6"),sQuery(id+"F0.wireOp",EDGE,"E7.filletArc"),sQuery(id+"F0.wireOp",EDGE,"E8.filletArc")])]}),"instanceName":"49"});
            var Q51;
            Q51=makeQuery(id+"F2.opPattern","COPY",BODY,{"derivedFrom":makeQuery(id+"F1.opExtrude","SWEPT_BODY",BODY,{"disambiguationData":[OSD([sQuery(id+"F0.wireOp",EDGE,"E0"),sQuery(id+"F0.wireOp",EDGE,"E1"),sQuery(id+"F0.wireOp",EDGE,"E2"),sQuery(id+"F0.wireOp",EDGE,"E3"),sQuery(id+"F0.wireOp",EDGE,"E4.filletArc"),sQuery(id+"F0.wireOp",EDGE,"E5"),sQuery(id+"F0.wireOp",EDGE,"E6"),sQuery(id+"F0.wireOp",EDGE,"E7.filletArc"),sQuery(id+"F0.wireOp",EDGE,"E8.filletArc")])]}),"instanceName":"50"});
            var Q52;
            Q52=makeQuery(id+"F2.opPattern","COPY",BODY,{"derivedFrom":makeQuery(id+"F1.opExtrude","SWEPT_BODY",BODY,{"disambiguationData":[OSD([sQuery(id+"F0.wireOp",EDGE,"E0"),sQuery(id+"F0.wireOp",EDGE,"E1"),sQuery(id+"F0.wireOp",EDGE,"E2"),sQuery(id+"F0.wireOp",EDGE,"E3"),sQuery(id+"F0.wireOp",EDGE,"E4.filletArc"),sQuery(id+"F0.wireOp",EDGE,"E5"),sQuery(id+"F0.wireOp",EDGE,"E6"),sQuery(id+"F0.wireOp",EDGE,"E7.filletArc"),sQuery(id+"F0.wireOp",EDGE,"E8.filletArc")])]}),"instanceName":"51"});
            var Q53;
            Q53=makeQuery(id+"F2.opPattern","COPY",BODY,{"derivedFrom":makeQuery(id+"F1.opExtrude","SWEPT_BODY",BODY,{"disambiguationData":[OSD([sQuery(id+"F0.wireOp",EDGE,"E0"),sQuery(id+"F0.wireOp",EDGE,"E1"),sQuery(id+"F0.wireOp",EDGE,"E2"),sQuery(id+"F0.wireOp",EDGE,"E3"),sQuery(id+"F0.wireOp",EDGE,"E4.filletArc"),sQuery(id+"F0.wireOp",EDGE,"E5"),sQuery(id+"F0.wireOp",EDGE,"E6"),sQuery(id+"F0.wireOp",EDGE,"E7.filletArc"),sQuery(id+"F0.wireOp",EDGE,"E8.filletArc")])]}),"instanceName":"52"});
            var Q54;
            Q54=makeQuery(id+"F2.opPattern","COPY",BODY,{"derivedFrom":makeQuery(id+"F1.opExtrude","SWEPT_BODY",BODY,{"disambiguationData":[OSD([sQuery(id+"F0.wireOp",EDGE,"E0"),sQuery(id+"F0.wireOp",EDGE,"E1"),sQuery(id+"F0.wireOp",EDGE,"E2"),sQuery(id+"F0.wireOp",EDGE,"E3"),sQuery(id+"F0.wireOp",EDGE,"E4.filletArc"),sQuery(id+"F0.wireOp",EDGE,"E5"),sQuery(id+"F0.wireOp",EDGE,"E6"),sQuery(id+"F0.wireOp",EDGE,"E7.filletArc"),sQuery(id+"F0.wireOp",EDGE,"E8.filletArc")])]}),"instanceName":"53"});
            var Q55;
            Q55=makeQuery(id+"F2.opPattern","COPY",BODY,{"derivedFrom":makeQuery(id+"F1.opExtrude","SWEPT_BODY",BODY,{"disambiguationData":[OSD([sQuery(id+"F0.wireOp",EDGE,"E0"),sQuery(id+"F0.wireOp",EDGE,"E1"),sQuery(id+"F0.wireOp",EDGE,"E2"),sQuery(id+"F0.wireOp",EDGE,"E3"),sQuery(id+"F0.wireOp",EDGE,"E4.filletArc"),sQuery(id+"F0.wireOp",EDGE,"E5"),sQuery(id+"F0.wireOp",EDGE,"E6"),sQuery(id+"F0.wireOp",EDGE,"E7.filletArc"),sQuery(id+"F0.wireOp",EDGE,"E8.filletArc")])]}),"instanceName":"54"});
            var Q56;
            Q56=makeQuery(id+"F2.opPattern","COPY",BODY,{"derivedFrom":makeQuery(id+"F1.opExtrude","SWEPT_BODY",BODY,{"disambiguationData":[OSD([sQuery(id+"F0.wireOp",EDGE,"E0"),sQuery(id+"F0.wireOp",EDGE,"E1"),sQuery(id+"F0.wireOp",EDGE,"E2"),sQuery(id+"F0.wireOp",EDGE,"E3"),sQuery(id+"F0.wireOp",EDGE,"E4.filletArc"),sQuery(id+"F0.wireOp",EDGE,"E5"),sQuery(id+"F0.wireOp",EDGE,"E6"),sQuery(id+"F0.wireOp",EDGE,"E7.filletArc"),sQuery(id+"F0.wireOp",EDGE,"E8.filletArc")])]}),"instanceName":"55"});
            var Q57;
            Q57=makeQuery(id+"F2.opPattern","COPY",BODY,{"derivedFrom":makeQuery(id+"F1.opExtrude","SWEPT_BODY",BODY,{"disambiguationData":[OSD([sQuery(id+"F0.wireOp",EDGE,"E0"),sQuery(id+"F0.wireOp",EDGE,"E1"),sQuery(id+"F0.wireOp",EDGE,"E2"),sQuery(id+"F0.wireOp",EDGE,"E3"),sQuery(id+"F0.wireOp",EDGE,"E4.filletArc"),sQuery(id+"F0.wireOp",EDGE,"E5"),sQuery(id+"F0.wireOp",EDGE,"E6"),sQuery(id+"F0.wireOp",EDGE,"E7.filletArc"),sQuery(id+"F0.wireOp",EDGE,"E8.filletArc")])]}),"instanceName":"56"});
            var Q58;
            Q58=makeQuery(id+"F2.opPattern","COPY",BODY,{"derivedFrom":makeQuery(id+"F1.opExtrude","SWEPT_BODY",BODY,{"disambiguationData":[OSD([sQuery(id+"F0.wireOp",EDGE,"E0"),sQuery(id+"F0.wireOp",EDGE,"E1"),sQuery(id+"F0.wireOp",EDGE,"E2"),sQuery(id+"F0.wireOp",EDGE,"E3"),sQuery(id+"F0.wireOp",EDGE,"E4.filletArc"),sQuery(id+"F0.wireOp",EDGE,"E5"),sQuery(id+"F0.wireOp",EDGE,"E6"),sQuery(id+"F0.wireOp",EDGE,"E7.filletArc"),sQuery(id+"F0.wireOp",EDGE,"E8.filletArc")])]}),"instanceName":"57"});
            var Q59;
            Q59=makeQuery(id+"F2.opPattern","COPY",BODY,{"derivedFrom":makeQuery(id+"F1.opExtrude","SWEPT_BODY",BODY,{"disambiguationData":[OSD([sQuery(id+"F0.wireOp",EDGE,"E0"),sQuery(id+"F0.wireOp",EDGE,"E1"),sQuery(id+"F0.wireOp",EDGE,"E2"),sQuery(id+"F0.wireOp",EDGE,"E3"),sQuery(id+"F0.wireOp",EDGE,"E4.filletArc"),sQuery(id+"F0.wireOp",EDGE,"E5"),sQuery(id+"F0.wireOp",EDGE,"E6"),sQuery(id+"F0.wireOp",EDGE,"E7.filletArc"),sQuery(id+"F0.wireOp",EDGE,"E8.filletArc")])]}),"instanceName":"58"});
            var Q60;
            Q60=makeQuery(id+"F2.opPattern","COPY",BODY,{"derivedFrom":makeQuery(id+"F1.opExtrude","SWEPT_BODY",BODY,{"disambiguationData":[OSD([sQuery(id+"F0.wireOp",EDGE,"E0"),sQuery(id+"F0.wireOp",EDGE,"E1"),sQuery(id+"F0.wireOp",EDGE,"E2"),sQuery(id+"F0.wireOp",EDGE,"E3"),sQuery(id+"F0.wireOp",EDGE,"E4.filletArc"),sQuery(id+"F0.wireOp",EDGE,"E5"),sQuery(id+"F0.wireOp",EDGE,"E6"),sQuery(id+"F0.wireOp",EDGE,"E7.filletArc"),sQuery(id+"F0.wireOp",EDGE,"E8.filletArc")])]}),"instanceName":"59"});
            var Q61;
            Q61=makeQuery(id+"F2.opPattern","COPY",BODY,{"derivedFrom":makeQuery(id+"F1.opExtrude","SWEPT_BODY",BODY,{"disambiguationData":[OSD([sQuery(id+"F0.wireOp",EDGE,"E0"),sQuery(id+"F0.wireOp",EDGE,"E1"),sQuery(id+"F0.wireOp",EDGE,"E2"),sQuery(id+"F0.wireOp",EDGE,"E3"),sQuery(id+"F0.wireOp",EDGE,"E4.filletArc"),sQuery(id+"F0.wireOp",EDGE,"E5"),sQuery(id+"F0.wireOp",EDGE,"E6"),sQuery(id+"F0.wireOp",EDGE,"E7.filletArc"),sQuery(id+"F0.wireOp",EDGE,"E8.filletArc")])]}),"instanceName":"60"});
            var Q62;
            Q62=makeQuery(id+"F2.opPattern","COPY",BODY,{"derivedFrom":makeQuery(id+"F1.opExtrude","SWEPT_BODY",BODY,{"disambiguationData":[OSD([sQuery(id+"F0.wireOp",EDGE,"E0"),sQuery(id+"F0.wireOp",EDGE,"E1"),sQuery(id+"F0.wireOp",EDGE,"E2"),sQuery(id+"F0.wireOp",EDGE,"E3"),sQuery(id+"F0.wireOp",EDGE,"E4.filletArc"),sQuery(id+"F0.wireOp",EDGE,"E5"),sQuery(id+"F0.wireOp",EDGE,"E6"),sQuery(id+"F0.wireOp",EDGE,"E7.filletArc"),sQuery(id+"F0.wireOp",EDGE,"E8.filletArc")])]}),"instanceName":"61"});
            var Q63;
            Q63=makeQuery(id+"F2.opPattern","COPY",BODY,{"derivedFrom":makeQuery(id+"F1.opExtrude","SWEPT_BODY",BODY,{"disambiguationData":[OSD([sQuery(id+"F0.wireOp",EDGE,"E0"),sQuery(id+"F0.wireOp",EDGE,"E1"),sQuery(id+"F0.wireOp",EDGE,"E2"),sQuery(id+"F0.wireOp",EDGE,"E3"),sQuery(id+"F0.wireOp",EDGE,"E4.filletArc"),sQuery(id+"F0.wireOp",EDGE,"E5"),sQuery(id+"F0.wireOp",EDGE,"E6"),sQuery(id+"F0.wireOp",EDGE,"E7.filletArc"),sQuery(id+"F0.wireOp",EDGE,"E8.filletArc")])]}),"instanceName":"62"});
            var Q64;
            Q64=makeQuery(id+"F2.opPattern","COPY",BODY,{"derivedFrom":makeQuery(id+"F1.opExtrude","SWEPT_BODY",BODY,{"disambiguationData":[OSD([sQuery(id+"F0.wireOp",EDGE,"E0"),sQuery(id+"F0.wireOp",EDGE,"E1"),sQuery(id+"F0.wireOp",EDGE,"E2"),sQuery(id+"F0.wireOp",EDGE,"E3"),sQuery(id+"F0.wireOp",EDGE,"E4.filletArc"),sQuery(id+"F0.wireOp",EDGE,"E5"),sQuery(id+"F0.wireOp",EDGE,"E6"),sQuery(id+"F0.wireOp",EDGE,"E7.filletArc"),sQuery(id+"F0.wireOp",EDGE,"E8.filletArc")])]}),"instanceName":"63"});
            var Q65;
            Q65=makeQuery(id+"F2.opPattern","COPY",BODY,{"derivedFrom":makeQuery(id+"F1.opExtrude","SWEPT_BODY",BODY,{"disambiguationData":[OSD([sQuery(id+"F0.wireOp",EDGE,"E0"),sQuery(id+"F0.wireOp",EDGE,"E1"),sQuery(id+"F0.wireOp",EDGE,"E2"),sQuery(id+"F0.wireOp",EDGE,"E3"),sQuery(id+"F0.wireOp",EDGE,"E4.filletArc"),sQuery(id+"F0.wireOp",EDGE,"E5"),sQuery(id+"F0.wireOp",EDGE,"E6"),sQuery(id+"F0.wireOp",EDGE,"E7.filletArc"),sQuery(id+"F0.wireOp",EDGE,"E8.filletArc")])]}),"instanceName":"64"});
            var Q66;
            Q66=makeQuery(id+"F2.opPattern","COPY",BODY,{"derivedFrom":makeQuery(id+"F1.opExtrude","SWEPT_BODY",BODY,{"disambiguationData":[OSD([sQuery(id+"F0.wireOp",EDGE,"E0"),sQuery(id+"F0.wireOp",EDGE,"E1"),sQuery(id+"F0.wireOp",EDGE,"E2"),sQuery(id+"F0.wireOp",EDGE,"E3"),sQuery(id+"F0.wireOp",EDGE,"E4.filletArc"),sQuery(id+"F0.wireOp",EDGE,"E5"),sQuery(id+"F0.wireOp",EDGE,"E6"),sQuery(id+"F0.wireOp",EDGE,"E7.filletArc"),sQuery(id+"F0.wireOp",EDGE,"E8.filletArc")])]}),"instanceName":"65"});
            var Q67;
            Q67=makeQuery(id+"F2.opPattern","COPY",BODY,{"derivedFrom":makeQuery(id+"F1.opExtrude","SWEPT_BODY",BODY,{"disambiguationData":[OSD([sQuery(id+"F0.wireOp",EDGE,"E0"),sQuery(id+"F0.wireOp",EDGE,"E1"),sQuery(id+"F0.wireOp",EDGE,"E2"),sQuery(id+"F0.wireOp",EDGE,"E3"),sQuery(id+"F0.wireOp",EDGE,"E4.filletArc"),sQuery(id+"F0.wireOp",EDGE,"E5"),sQuery(id+"F0.wireOp",EDGE,"E6"),sQuery(id+"F0.wireOp",EDGE,"E7.filletArc"),sQuery(id+"F0.wireOp",EDGE,"E8.filletArc")])]}),"instanceName":"66"});
            var Q68;
            Q68=makeQuery(id+"F2.opPattern","COPY",BODY,{"derivedFrom":makeQuery(id+"F1.opExtrude","SWEPT_BODY",BODY,{"disambiguationData":[OSD([sQuery(id+"F0.wireOp",EDGE,"E0"),sQuery(id+"F0.wireOp",EDGE,"E1"),sQuery(id+"F0.wireOp",EDGE,"E2"),sQuery(id+"F0.wireOp",EDGE,"E3"),sQuery(id+"F0.wireOp",EDGE,"E4.filletArc"),sQuery(id+"F0.wireOp",EDGE,"E5"),sQuery(id+"F0.wireOp",EDGE,"E6"),sQuery(id+"F0.wireOp",EDGE,"E7.filletArc"),sQuery(id+"F0.wireOp",EDGE,"E8.filletArc")])]}),"instanceName":"67"});
            var Q69;
            Q69=makeQuery(id+"F2.opPattern","COPY",BODY,{"derivedFrom":makeQuery(id+"F1.opExtrude","SWEPT_BODY",BODY,{"disambiguationData":[OSD([sQuery(id+"F0.wireOp",EDGE,"E0"),sQuery(id+"F0.wireOp",EDGE,"E1"),sQuery(id+"F0.wireOp",EDGE,"E2"),sQuery(id+"F0.wireOp",EDGE,"E3"),sQuery(id+"F0.wireOp",EDGE,"E4.filletArc"),sQuery(id+"F0.wireOp",EDGE,"E5"),sQuery(id+"F0.wireOp",EDGE,"E6"),sQuery(id+"F0.wireOp",EDGE,"E7.filletArc"),sQuery(id+"F0.wireOp",EDGE,"E8.filletArc")])]}),"instanceName":"68"});
            var Q70;
            Q70=makeQuery(id+"F2.opPattern","COPY",BODY,{"derivedFrom":makeQuery(id+"F1.opExtrude","SWEPT_BODY",BODY,{"disambiguationData":[OSD([sQuery(id+"F0.wireOp",EDGE,"E0"),sQuery(id+"F0.wireOp",EDGE,"E1"),sQuery(id+"F0.wireOp",EDGE,"E2"),sQuery(id+"F0.wireOp",EDGE,"E3"),sQuery(id+"F0.wireOp",EDGE,"E4.filletArc"),sQuery(id+"F0.wireOp",EDGE,"E5"),sQuery(id+"F0.wireOp",EDGE,"E6"),sQuery(id+"F0.wireOp",EDGE,"E7.filletArc"),sQuery(id+"F0.wireOp",EDGE,"E8.filletArc")])]}),"instanceName":"69"});
            var Q71;
            Q71=makeQuery(id+"F2.opPattern","COPY",BODY,{"derivedFrom":makeQuery(id+"F1.opExtrude","SWEPT_BODY",BODY,{"disambiguationData":[OSD([sQuery(id+"F0.wireOp",EDGE,"E0"),sQuery(id+"F0.wireOp",EDGE,"E1"),sQuery(id+"F0.wireOp",EDGE,"E2"),sQuery(id+"F0.wireOp",EDGE,"E3"),sQuery(id+"F0.wireOp",EDGE,"E4.filletArc"),sQuery(id+"F0.wireOp",EDGE,"E5"),sQuery(id+"F0.wireOp",EDGE,"E6"),sQuery(id+"F0.wireOp",EDGE,"E7.filletArc"),sQuery(id+"F0.wireOp",EDGE,"E8.filletArc")])]}),"instanceName":"70"});
            var Q72;
            Q72=makeQuery(id+"F2.opPattern","COPY",BODY,{"derivedFrom":makeQuery(id+"F1.opExtrude","SWEPT_BODY",BODY,{"disambiguationData":[OSD([sQuery(id+"F0.wireOp",EDGE,"E0"),sQuery(id+"F0.wireOp",EDGE,"E1"),sQuery(id+"F0.wireOp",EDGE,"E2"),sQuery(id+"F0.wireOp",EDGE,"E3"),sQuery(id+"F0.wireOp",EDGE,"E4.filletArc"),sQuery(id+"F0.wireOp",EDGE,"E5"),sQuery(id+"F0.wireOp",EDGE,"E6"),sQuery(id+"F0.wireOp",EDGE,"E7.filletArc"),sQuery(id+"F0.wireOp",EDGE,"E8.filletArc")])]}),"instanceName":"71"});
            hole(context, id + "F3", {"style" : HoleStyle.SIMPLE, "endStyle" : HoleEndStyle.THROUGH, "oppositeDirection" : true, "holeDiameter" : 12.7 * mm, "majorDiameter" : 6.35 * mm, "isTappedThrough" : true, "tappedDepth" : 12.7 * mm, "tapClearance" : 3, "locations" : qUnion([Q0]), "scope" : qUnion([Q1, Q2, Q3, Q4, Q5, Q6, Q7, Q8, Q9, Q10, Q11, Q12, Q13, Q14, Q15, Q16, Q17, Q18, Q19, Q20, Q21, Q22, Q23, Q24, Q25, Q26, Q27, Q28, Q29, Q30, Q31, Q32, Q33, Q34, Q35, Q36, Q37, Q38, Q39, Q40, Q41, Q42, Q43, Q44, Q45, Q46, Q47, Q48, Q49, Q50, Q51, Q52, Q53, Q54, Q55, Q56, Q57, Q58, Q59, Q60, Q61, Q62, Q63, Q64, Q65, Q66, Q67, Q68, Q69, Q70, Q71, Q72])});
        }
    });
